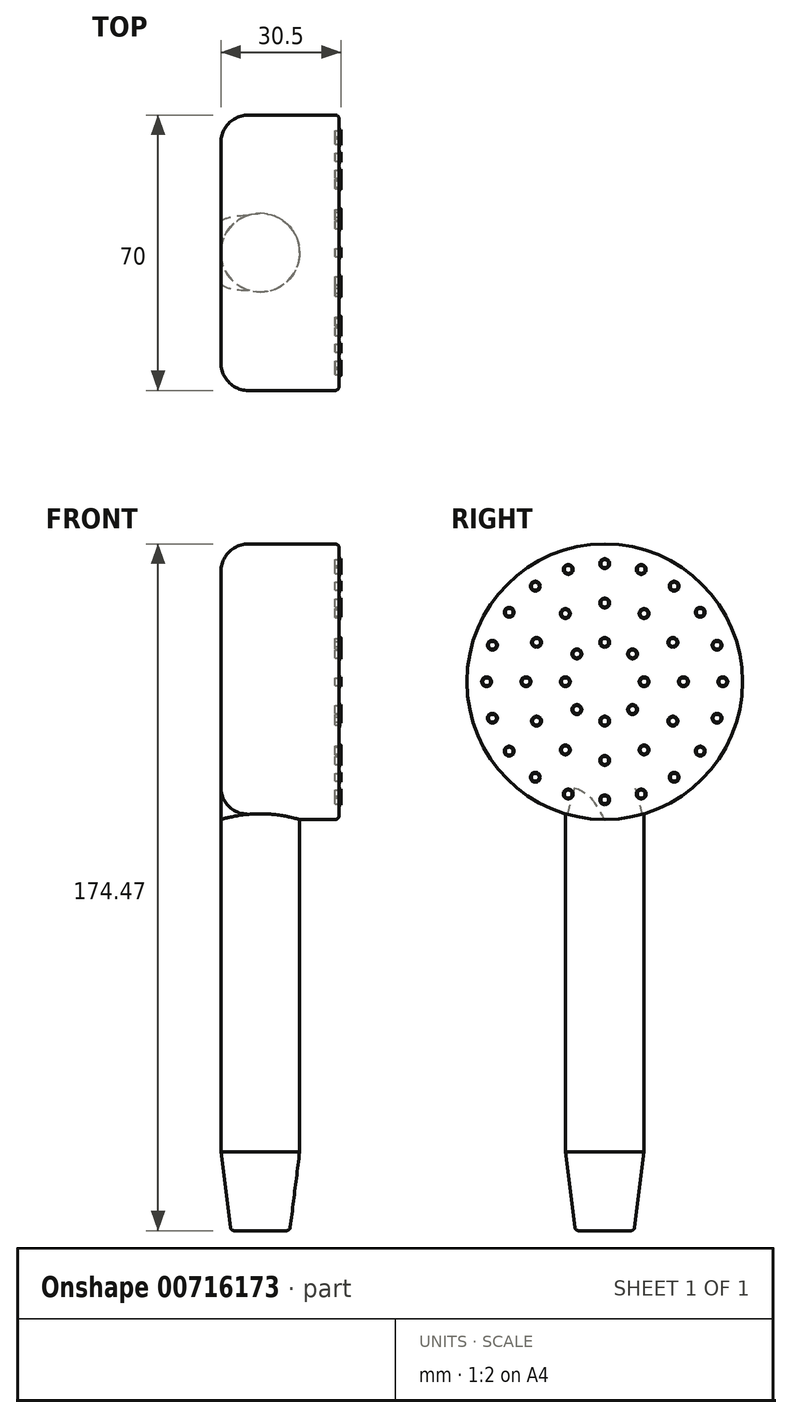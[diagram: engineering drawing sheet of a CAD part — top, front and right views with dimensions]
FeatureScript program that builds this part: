
annotation { "Feature Type Name" : "Feature", "Feature Type Description" : "" }
export const myFeature = defineFeature(function(context is Context, id is Id, definition is map)
    precondition{}
    {
        {
            var Q0;
            Q0=qCreatedBy(makeId("Top.planeOp"),FACE);
            var sketch = newSketch(context, id + "F0", { "sketchPlane" : qUnion([Q0])});
            skCircle(sketch, "E0", {"center": v(0, 0) * mm, "radius": 10 * mm});
            skSolve(sketch);
        }
        {
            var Q0;
            Q0 = qSketchRegion(id + "F0", true);
            extrude(context, id + "F1", {"entities" : qUnion([Q0]), "depth" : 100 * mm, "offsetDistance" : 25 * mm});
        }
        {
            var Q0;
            Q0=qCreatedBy(makeId("Right.planeOp"),FACE);
            var sketch = newSketch(context, id + "F2", { "sketchPlane" : qUnion([Q0])});
            skCircle(sketch, "E1", {"center": v(0, 119.47) * mm, "radius": 35 * mm});
            skSolve(sketch);
        }
        {
            var Q0;
            Q0 = qSketchRegion(id + "F2", true);
            extrude(context, id + "F3", {"entities" : qUnion([Q0]), "operationType" : NewBodyOperationType.ADD, "oppositeDirection" : true, "depth" : 10 * mm, "offsetDistance" : 25 * mm});
        }
        {
            var Q0;
            Q0 = qSketchRegion(id + "F2", true);
            extrude(context, id + "F4", {"entities" : qUnion([Q0]), "operationType" : NewBodyOperationType.ADD, "depth" : 20 * mm, "offsetDistance" : 25 * mm});
        }
        {
            var Q0;
            Q0=makeQuery(id+"F4.opExtrude","CAP_FACE",FACE,{"disambiguationData":[OSD([sQuery(id+"F2.wireOp",EDGE,"E1")])],"isStart":false});
            var sketch = newSketch(context, id + "F5", { "sketchPlane" : qUnion([Q0])});
            skPoint(sketch, "E2.center", {"position": v(0, 119.47) * mm});
            skCircle(sketch, "E3", {"center": v(0, 149.47) * mm, "radius": 1 * mm});
            skCircle(sketch, "E4.1.0", {"center": v(-9.27, 148) * mm, "radius": 1 * mm});
            skCircle(sketch, "E4.2.0", {"center": v(-17.63, 143.74) * mm, "radius": 1 * mm});
            skCircle(sketch, "E5.1.3.0", {"center": v(-24.27, 137.1) * mm, "radius": 1 * mm});
            skCircle(sketch, "E5.1.4.0", {"center": v(-28.53, 128.74) * mm, "radius": 1 * mm});
            skCircle(sketch, "E5.1.5.0", {"center": v(-30, 119.47) * mm, "radius": 1 * mm});
            skCircle(sketch, "E5.1.6.0", {"center": v(-28.53, 110.2) * mm, "radius": 1 * mm});
            skCircle(sketch, "E5.1.7.0", {"center": v(-24.27, 101.83) * mm, "radius": 1 * mm});
            skCircle(sketch, "E5.1.8.0", {"center": v(-17.63, 95.2) * mm, "radius": 1 * mm});
            skCircle(sketch, "E5.1.9.0", {"center": v(-9.27, 90.94) * mm, "radius": 1 * mm});
            skCircle(sketch, "E5.1.10.0", {"center": v(0, 89.47) * mm, "radius": 1 * mm});
            skCircle(sketch, "E5.1.11.0", {"center": v(9.27, 90.94) * mm, "radius": 1 * mm});
            skCircle(sketch, "E5.1.12.0", {"center": v(17.63, 95.2) * mm, "radius": 1 * mm});
            skCircle(sketch, "E5.1.13.0", {"center": v(24.27, 101.83) * mm, "radius": 1 * mm});
            skCircle(sketch, "E5.1.14.0", {"center": v(28.53, 110.2) * mm, "radius": 1 * mm});
            skCircle(sketch, "E5.1.15.0", {"center": v(30, 119.47) * mm, "radius": 1 * mm});
            skCircle(sketch, "E5.1.16.0", {"center": v(28.53, 128.74) * mm, "radius": 1 * mm});
            skCircle(sketch, "E5.1.17.0", {"center": v(24.27, 137.1) * mm, "radius": 1 * mm});
            skCircle(sketch, "E5.1.18.0", {"center": v(17.63, 143.74) * mm, "radius": 1 * mm});
            skCircle(sketch, "E5.1.19.0", {"center": v(9.27, 148) * mm, "radius": 1 * mm});
            skCircle(sketch, "E6", {"center": v(0, 139.47) * mm, "radius": 1 * mm});
            skCircle(sketch, "E7", {"center": v(0, 129.47) * mm, "radius": 1 * mm});
            skCircle(sketch, "E8.1.0", {"center": v(-10, 136.79) * mm, "radius": 1 * mm});
            skCircle(sketch, "E8.2.0", {"center": v(-17.32, 129.47) * mm, "radius": 1 * mm});
            skCircle(sketch, "E9.1.3.0", {"center": v(-20, 119.47) * mm, "radius": 1 * mm});
            skCircle(sketch, "E9.1.4.0", {"center": v(-17.32, 109.47) * mm, "radius": 1 * mm});
            skCircle(sketch, "E9.1.5.0", {"center": v(-10, 102.15) * mm, "radius": 1 * mm});
            skCircle(sketch, "E9.1.6.0", {"center": v(0, 99.47) * mm, "radius": 1 * mm});
            skCircle(sketch, "E9.1.7.0", {"center": v(10, 102.15) * mm, "radius": 1 * mm});
            skCircle(sketch, "E9.1.8.0", {"center": v(17.32, 109.47) * mm, "radius": 1 * mm});
            skCircle(sketch, "E9.1.9.0", {"center": v(20, 119.47) * mm, "radius": 1 * mm});
            skCircle(sketch, "E10.1.10.0", {"center": v(17.32, 129.47) * mm, "radius": 1 * mm});
            skCircle(sketch, "E10.1.11.0", {"center": v(10, 136.79) * mm, "radius": 1 * mm});
            skCircle(sketch, "E11.1.0", {"center": v(-7.07, 126.54) * mm, "radius": 1 * mm});
            skCircle(sketch, "E11.2.0", {"center": v(-10, 119.47) * mm, "radius": 1 * mm});
            skCircle(sketch, "E12.1.3.0", {"center": v(-7.07, 112.4) * mm, "radius": 1 * mm});
            skCircle(sketch, "E12.1.4.0", {"center": v(0, 109.47) * mm, "radius": 1 * mm});
            skCircle(sketch, "E12.1.5.0", {"center": v(7.07, 112.4) * mm, "radius": 1 * mm});
            skCircle(sketch, "E13.1.6.0", {"center": v(10, 119.47) * mm, "radius": 1 * mm});
            skCircle(sketch, "E13.1.7.0", {"center": v(7.07, 126.54) * mm, "radius": 1 * mm});
            skSolve(sketch);
        }
        {
            var Q0;
            Q0 = qSketchRegion(id + "F5", true);
            extrude(context, id + "F6", {"entities" : qUnion([Q0]), "operationType" : NewBodyOperationType.REMOVE, "oppositeDirection" : true, "depth" : 1 * mm, "offsetDistance" : 25 * mm});
        }
        {
            var Q0;
            Q0=makeQuery(id+"F3.opExtrude","CAP_EDGE",EDGE,{"disambiguationData":[OSD([sQuery(id+"F2.wireOp",EDGE,"E1")])],"isStart":false});
            fillet(context, id + "F7", {"entities" : qUnion([Q0]), "radius" : 7 * mm, "tangentPropagation" : true, "allowEdgeOverflow" : false});
        }
        {
            var Q0;
            Q0=makeQuery(id+"F4.opExtrude","CAP_EDGE",EDGE,{"disambiguationData":[OSD([sQuery(id+"F2.wireOp",EDGE,"E1")])],"isStart":false});
            fillet(context, id + "F8", {"entities" : qUnion([Q0]), "radius" : 1 * mm, "tangentPropagation" : true, "allowEdgeOverflow" : false});
        }
        {
            var Q0;
            Q0=qCreatedBy(makeId("Top.planeOp"),FACE);
            cPlane(context, id + "F9", {"entities" : qUnion([Q0]), "cplaneType" : CPlaneType.OFFSET, "offset" : 20 * mm, "oppositeDirection" : true, "width" : 150 * mm, "height" : 150 * mm});
        }
        {
            var Q0;
            Q0=qCreatedBy(id+"F9.planeOp",FACE);
            var sketch = newSketch(context, id + "F10", { "sketchPlane" : qUnion([Q0])});
            skCircle(sketch, "E14", {"center": v(0, 0) * mm, "radius": 7.5 * mm});
            skSolve(sketch);
        }
        {
            var Q1;
            Q1=makeQuery(id+"F1.opExtrude","CAP_FACE",FACE,{"disambiguationData":[OSD([sQuery(id+"F0.wireOp",EDGE,"E0")])],"isStart":true});
            var Q2;
            Q2=makeQuery(id+"F10.imprint","IMPRINT",FACE,{"disambiguationData":[TD([[makeQuery(id+"F10.imprint","IMPRINT",EDGE,{"derivedFrom":sQuery(id+"F10.wireOp",EDGE,"E14")}),1.0]])]});
            loft(context, id + "F11", {"operationType" : NewBodyOperationType.ADD, "sheetProfilesArray" : [{ "sheetProfileEntities" : qUnion([Q1]) }, { "sheetProfileEntities" : qUnion([Q2]) }]});
        }
        {
            var Q0;
            Q0=makeQuery(id+"F11.opLoft","MID_CAP_EDGE",EDGE,{"disambiguationData":[OSD([sQuery(id+"F10.wireOp",EDGE,"E14")])],"capPos":1.0});
            fillet(context, id + "F12", {"entities" : qUnion([Q0]), "radius" : 1 * mm, "tangentPropagation" : true, "allowEdgeOverflow" : false});
        }
        {
            var Q0;
            Q0=makeQuery(id+"F4.opExtrude","CAP_FACE",FACE,{"disambiguationData":[OSD([sQuery(id+"F2.wireOp",EDGE,"E1")])],"isStart":false});
            var sketch = newSketch(context, id + "F13", { "sketchPlane" : qUnion([Q0])});
            skCircle(sketch, "E15", {"center": v(0, 129.47) * mm, "radius": 1.25 * mm});
            skCircle(sketch, "E16.1.0", {"center": v(-7.07, 126.54) * mm, "radius": 1.25 * mm});
            skCircle(sketch, "E16.2.0", {"center": v(-10, 119.47) * mm, "radius": 1.25 * mm});
            skPoint(sketch, "E16.center", {"position": v(0, 119.47) * mm});
            skCircle(sketch, "E17.1.3.0", {"center": v(-7.07, 112.4) * mm, "radius": 1.25 * mm});
            skCircle(sketch, "E17.1.4.0", {"center": v(0, 109.47) * mm, "radius": 1.25 * mm});
            skCircle(sketch, "E17.1.5.0", {"center": v(7.07, 112.4) * mm, "radius": 1.25 * mm});
            skCircle(sketch, "E17.1.6.0", {"center": v(10, 119.47) * mm, "radius": 1.25 * mm});
            skCircle(sketch, "E17.1.7.0", {"center": v(7.07, 126.54) * mm, "radius": 1.25 * mm});
            skCircle(sketch, "E18", {"center": v(0, 139.47) * mm, "radius": 1.25 * mm});
            skCircle(sketch, "E19.1.0", {"center": v(-10, 136.79) * mm, "radius": 1.25 * mm});
            skCircle(sketch, "E19.2.0", {"center": v(-17.32, 129.47) * mm, "radius": 1.25 * mm});
            skCircle(sketch, "E20.1.3.0", {"center": v(-20, 119.47) * mm, "radius": 1.25 * mm});
            skCircle(sketch, "E20.1.4.0", {"center": v(-17.32, 109.47) * mm, "radius": 1.25 * mm});
            skCircle(sketch, "E20.1.5.0", {"center": v(-10, 102.15) * mm, "radius": 1.25 * mm});
            skCircle(sketch, "E20.1.6.0", {"center": v(0, 99.47) * mm, "radius": 1.25 * mm});
            skCircle(sketch, "E20.1.7.0", {"center": v(10, 102.15) * mm, "radius": 1.25 * mm});
            skCircle(sketch, "E20.1.8.0", {"center": v(17.32, 109.47) * mm, "radius": 1.25 * mm});
            skCircle(sketch, "E20.1.9.0", {"center": v(20, 119.47) * mm, "radius": 1.25 * mm});
            skCircle(sketch, "E20.1.10.0", {"center": v(17.32, 129.47) * mm, "radius": 1.25 * mm});
            skCircle(sketch, "E20.1.11.0", {"center": v(10, 136.79) * mm, "radius": 1.25 * mm});
            skCircle(sketch, "E21", {"center": v(0, 149.47) * mm, "radius": 1.25 * mm});
            skCircle(sketch, "E22.1.0", {"center": v(-9.27, 148) * mm, "radius": 1.25 * mm});
            skCircle(sketch, "E23.1.2.0", {"center": v(-17.63, 143.74) * mm, "radius": 1.25 * mm});
            skCircle(sketch, "E23.1.3.0", {"center": v(-24.27, 137.1) * mm, "radius": 1.25 * mm});
            skCircle(sketch, "E23.1.4.0", {"center": v(-28.53, 128.74) * mm, "radius": 1.25 * mm});
            skCircle(sketch, "E23.1.5.0", {"center": v(-30, 119.47) * mm, "radius": 1.25 * mm});
            skCircle(sketch, "E23.1.6.0", {"center": v(-28.53, 110.2) * mm, "radius": 1.25 * mm});
            skCircle(sketch, "E23.1.7.0", {"center": v(-24.27, 101.83) * mm, "radius": 1.25 * mm});
            skCircle(sketch, "E23.1.8.0", {"center": v(-17.63, 95.2) * mm, "radius": 1.25 * mm});
            skCircle(sketch, "E23.1.9.0", {"center": v(-9.27, 90.94) * mm, "radius": 1.25 * mm});
            skCircle(sketch, "E23.1.10.0", {"center": v(0, 89.47) * mm, "radius": 1.25 * mm});
            skCircle(sketch, "E23.1.11.0", {"center": v(9.27, 90.94) * mm, "radius": 1.25 * mm});
            skCircle(sketch, "E23.1.12.0", {"center": v(17.63, 95.2) * mm, "radius": 1.25 * mm});
            skCircle(sketch, "E23.1.13.0", {"center": v(24.27, 101.83) * mm, "radius": 1.25 * mm});
            skCircle(sketch, "E23.1.14.0", {"center": v(28.53, 110.2) * mm, "radius": 1.25 * mm});
            skCircle(sketch, "E23.1.15.0", {"center": v(30, 119.47) * mm, "radius": 1.25 * mm});
            skCircle(sketch, "E23.1.16.0", {"center": v(28.53, 128.74) * mm, "radius": 1.25 * mm});
            skCircle(sketch, "E23.1.17.0", {"center": v(24.27, 137.1) * mm, "radius": 1.25 * mm});
            skCircle(sketch, "E23.1.18.0", {"center": v(17.63, 143.74) * mm, "radius": 1.25 * mm});
            skCircle(sketch, "E23.1.19.0", {"center": v(9.27, 148) * mm, "radius": 1.25 * mm});
            skSolve(sketch);
        }
        {
            var Q0;
            Q0 = qSketchRegion(id + "F13", true);
            extrude(context, id + "F14", {"entities" : qUnion([Q0]), "operationType" : NewBodyOperationType.ADD, "depth" : 0.5 * mm, "offsetDistance" : 25 * mm});
        }
        {
            var Q0;
            Q0 = qSketchRegion(id + "F5", true);
            extrude(context, id + "F15", {"entities" : qUnion([Q0]), "operationType" : NewBodyOperationType.REMOVE, "depth" : 1 * mm, "offsetDistance" : 25 * mm});
        }
    });
